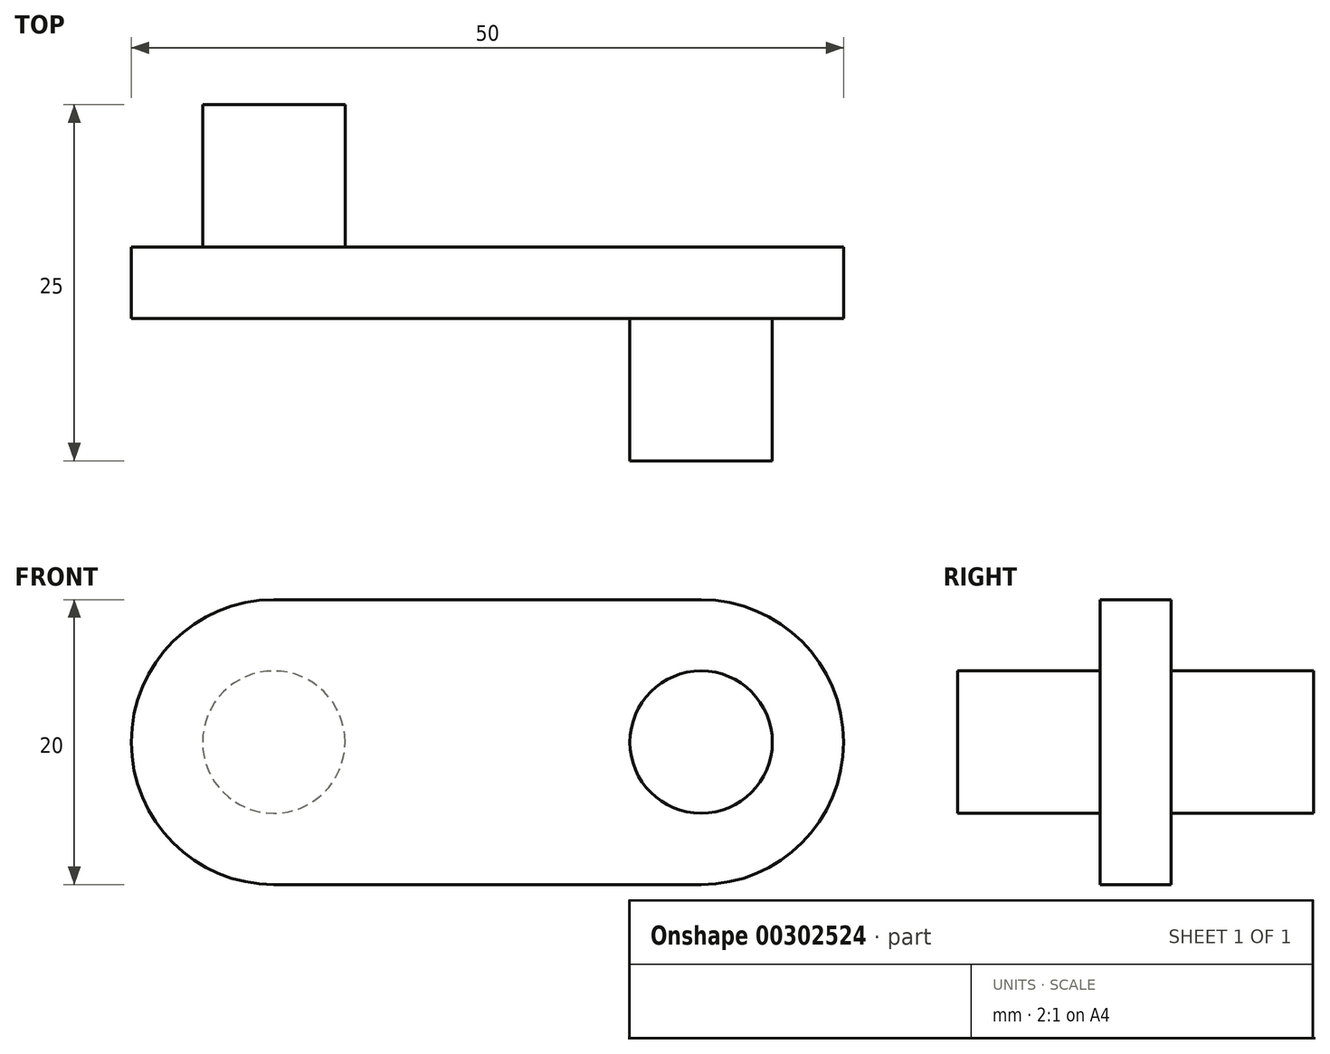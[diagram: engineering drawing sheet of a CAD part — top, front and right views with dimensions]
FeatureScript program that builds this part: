
annotation { "Feature Type Name" : "Feature", "Feature Type Description" : "" }
export const myFeature = defineFeature(function(context is Context, id is Id, definition is map)
    precondition{}
    {
        {
            var Q0;
            Q0=qCreatedBy(makeId("Front.planeOp"),FACE);
            var sketch = newSketch(context, id + "F0", { "sketchPlane" : qUnion([Q0])});
            skLineSegment(sketch, "E0", {"start": v(0, 20) * mm, "end": v(30, 20) * mm});
            skLineSegment(sketch, "E1", {"start": v(0, 0) * mm, "end": v(30, 0) * mm});
            skArc(sketch, "E2", {"start": v(0, 20) * mm, "mid": v(-10, 10) * mm, "end": v(0, 0) * mm});
            skArc(sketch, "E3", {"start": v(30, 0) * mm, "mid": v(40, 10) * mm, "end": v(30, 20) * mm});
            skSolve(sketch);
        }
        {
            var Q0;
            Q0 = qSketchRegion(id + "F0", true);
            extrude(context, id + "F1", {"entities" : qUnion([Q0]), "depth" : 5 * mm});
        }
        {
            var Q0;
            Q0=makeQuery(id+"F1.opExtrude","CAP_FACE",FACE,{"disambiguationData":[OSD([sQuery(id+"F0.wireOp",EDGE,"E0"),sQuery(id+"F0.wireOp",EDGE,"E1"),sQuery(id+"F0.wireOp",EDGE,"E2"),sQuery(id+"F0.wireOp",EDGE,"E3")])],"isStart":false});
            var sketch = newSketch(context, id + "F2", { "sketchPlane" : qUnion([Q0])});
            skCircle(sketch, "E4", {"center": v(30, 10) * mm, "radius": 5 * mm});
            skSolve(sketch);
        }
        {
            var Q0;
            Q0 = qSketchRegion(id + "F2", true);
            extrude(context, id + "F3", {"entities" : qUnion([Q0]), "operationType" : NewBodyOperationType.ADD, "depth" : 10 * mm});
        }
        {
            var Q0;
            Q0=makeQuery(id+"F0.imprint","IMPRINT",FACE,{"disambiguationData":[TD([[makeQuery(id+"F0.imprint","IMPRINT",EDGE,{"derivedFrom":sQuery(id+"F0.wireOp",EDGE,"E0")}),-1.0]])]});
            var sketch = newSketch(context, id + "F4", { "sketchPlane" : qUnion([Q0])});
            skCircle(sketch, "E5", {"center": v(0, 10) * mm, "radius": 5 * mm});
            skSolve(sketch);
        }
        {
            var Q0;
            Q0=makeQuery(id+"F4.imprint","IMPRINT",FACE,{"disambiguationData":[TD([[makeQuery(id+"F4.imprint","IMPRINT",EDGE,{"derivedFrom":sQuery(id+"F4.wireOp",EDGE,"E5")}),1.0]])]});
            var Q1;
            Q1=sQuery(id+"F4.wireOp",EDGE,"E5");
            extrude(context, id + "F5", {"entities" : qUnion([Q0]), "operationType" : NewBodyOperationType.ADD, "surfaceEntities" : qUnion([Q1]), "oppositeDirection" : true, "depth" : 10 * mm});
        }
    });
